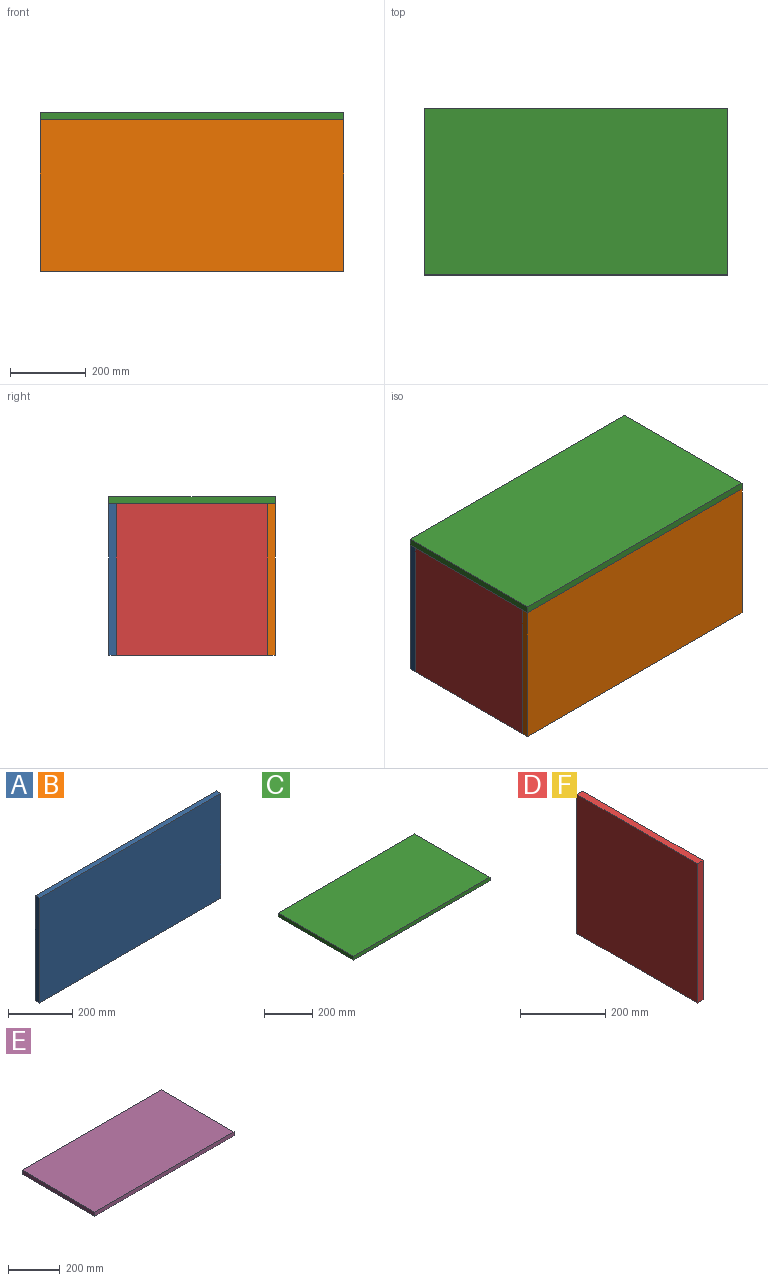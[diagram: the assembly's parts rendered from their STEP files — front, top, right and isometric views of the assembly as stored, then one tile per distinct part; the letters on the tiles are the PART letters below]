
ASSEMBLY  parts=6 mates=5
PART A: 6 faces, bbox 800x19x400 mm
  f0: plane 800x19mm, normal (0,0,-1), area 15200mm2, adj f1,f3,f4,f5
  f1: plane 400x19mm, normal (1,0,0), area 7600mm2, adj f0,f2,f4,f5
  f2: plane 800x19mm, normal (0,0,1), area 15200mm2, adj f1,f3,f4,f5
  f3: plane 400x19mm, normal (-1,0,0), area 7600mm2, adj f0,f2,f4,f5
  f4: plane 800x400mm, normal (0,-1,0), area 320000mm2, adj f0,f1,f2,f3
  f5: plane 800x400mm, normal (0,1,0), area 320000mm2, adj f0,f1,f2,f3
PART B: same geometry as A
PART C: 6 faces, bbox 800x438x19 mm
  f0: plane 800x19mm, normal (0,-1,0), area 15200mm2, adj f1,f3,f4,f5
  f1: plane 438x19mm, normal (1,0,0), area 8322mm2, adj f0,f2,f4,f5
  f2: plane 800x19mm, normal (0,1,0), area 15200mm2, adj f1,f3,f4,f5
  f3: plane 438x19mm, normal (-1,0,0), area 8322mm2, adj f0,f2,f4,f5
  f4: plane 800x438mm, normal (0,0,1), area 350400mm2, adj f0,f1,f2,f3
  f5: plane 800x438mm, normal (0,0,-1), area 350400mm2, adj f0,f1,f2,f3
PART D: 6 faces, bbox 19x400x400 mm
  f0: plane 400x19mm, normal (0,0,-1), area 7600mm2, adj f1,f3,f4,f5
  f1: plane 400x400mm, normal (-1,0,0), area 160000mm2, adj f0,f2,f4,f5
  f2: plane 400x19mm, normal (0,0,1), area 7600mm2, adj f1,f3,f4,f5
  f3: plane 400x400mm, normal (1,0,0), area 160000mm2, adj f0,f2,f4,f5
  f4: plane 400x19mm, normal (0,1,0), area 7600mm2, adj f0,f1,f2,f3
  f5: plane 400x19mm, normal (0,-1,0), area 7600mm2, adj f0,f1,f2,f3
PART E: 6 faces, bbox 762x400x19 mm
  f0: plane 762x400mm, normal (0,0,1), area 304800mm2, adj f1,f3,f4,f5
  f1: plane 400x19mm, normal (1,0,0), area 7600mm2, adj f0,f2,f4,f5
  f2: plane 762x400mm, normal (0,0,-1), area 304800mm2, adj f1,f3,f4,f5
  f3: plane 400x19mm, normal (-1,0,0), area 7600mm2, adj f0,f2,f4,f5
  f4: plane 762x19mm, normal (0,1,0), area 14478mm2, adj f0,f1,f2,f3
  f5: plane 762x19mm, normal (0,-1,0), area 14478mm2, adj f0,f1,f2,f3
PART F: same geometry as D
PLACE A t=(-658.27,-227.54,491.7)mm
PLACE B t=(-658.27,-646.54,491.7)mm
PLACE C t=(-658.27,-665.54,891.7)mm
PLACE D t=(-1439.27,-646.54,491.7)mm
PLACE E t=(-639.27,-646.54,491.7)mm
PLACE F t=(-658.27,-646.54,491.7)mm
MATE fastened A.f4 <-> F.f4  axis (0,-1,0) through (-658.27,-246.54,891.7)mm
MATE fastened A.f4 <-> E.f4  axis (0,-1,0) through (-1458.27,-246.54,491.7)mm
MATE fastened D.f5 <-> B.f5  axis (0,-1,0) through (-1458.27,-646.54,891.7)mm
MATE fastened C.f5 <-> A.f2  axis (0,0,-1) through (-658.27,-227.54,891.7)mm
MATE fastened D.f4 <-> A.f4  axis (0,1,0) through (-1458.27,-246.54,891.7)mm
